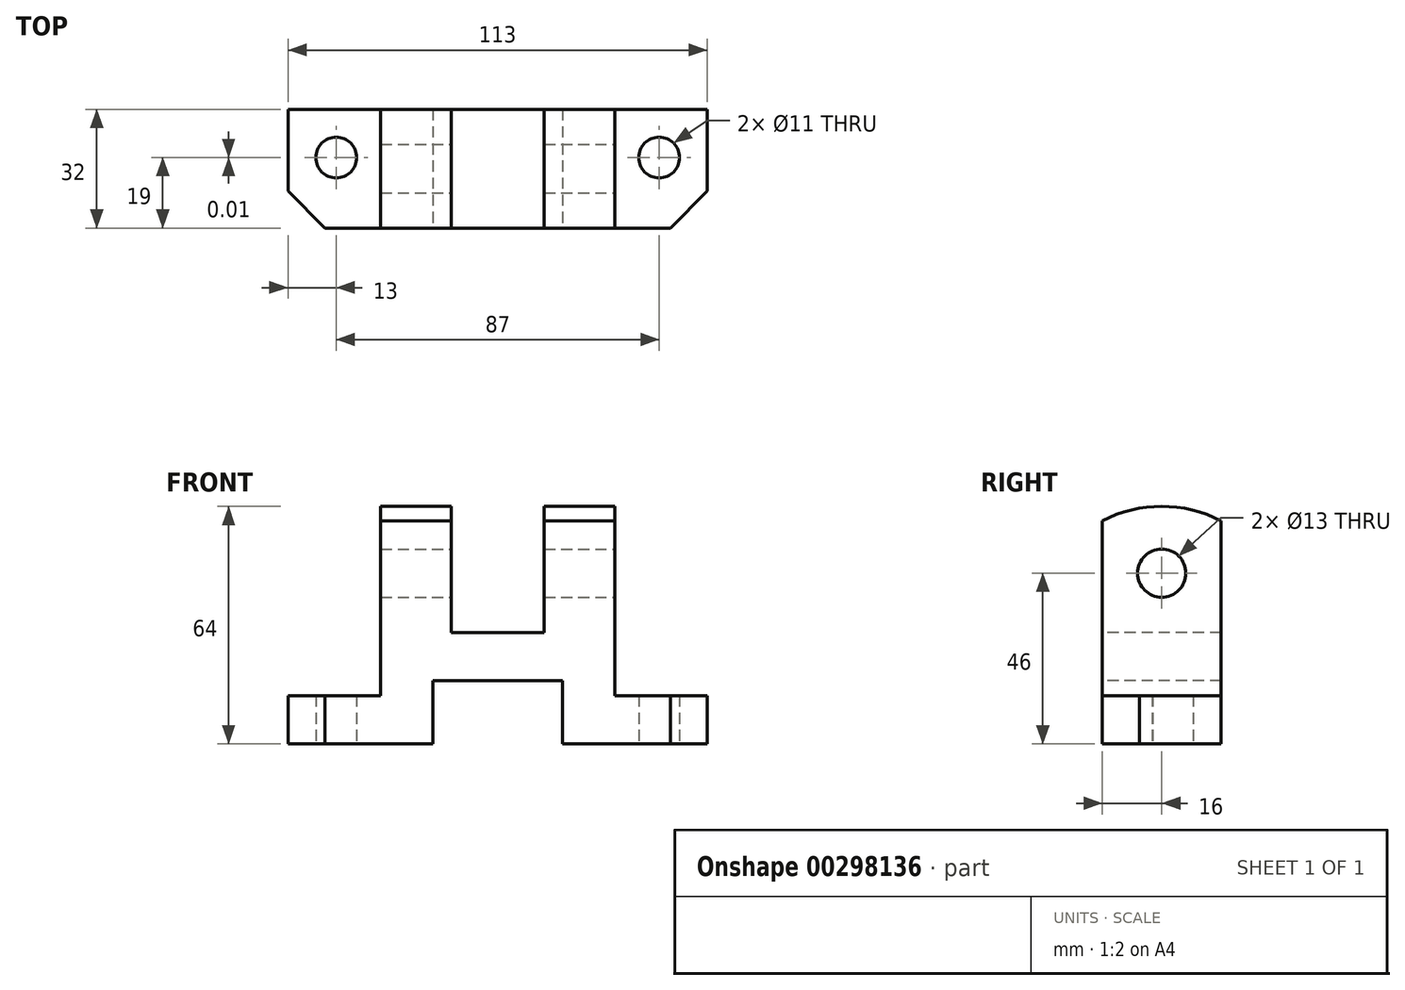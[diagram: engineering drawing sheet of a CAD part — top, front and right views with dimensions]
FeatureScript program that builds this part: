
annotation { "Feature Type Name" : "Feature", "Feature Type Description" : "" }
export const myFeature = defineFeature(function(context is Context, id is Id, definition is map)
    precondition{}
    {
        {
            var Q0;
            Q0=qCreatedBy(makeId("Front.planeOp"),FACE);
            var sketch = newSketch(context, id + "F0", { "sketchPlane" : qUnion([Q0])});
            skLineSegment(sketch, "E0", {"start": v(0, 0) * mm, "end": v(113, 0) * mm});
            skLineSegment(sketch, "E1", {"start": v(113, 0) * mm, "end": v(113, 64) * mm});
            skLineSegment(sketch, "E2", {"start": v(113, 64) * mm, "end": v(0, 64) * mm});
            skLineSegment(sketch, "E3", {"start": v(0, 64) * mm, "end": v(0, 0) * mm});
            skSolve(sketch);
        }
        {
            var Q0;
            Q0 = qSketchRegion(id + "F0", true);
            extrude(context, id + "F1", {"entities" : qUnion([Q0]), "depth" : 32 * mm});
        }
        {
            var Q0;
            Q0=makeQuery(id+"F1.opExtrude","CAP_FACE",FACE,{"disambiguationData":[OSD([sQuery(id+"F0.wireOp",EDGE,"E0"),sQuery(id+"F0.wireOp",EDGE,"E1"),sQuery(id+"F0.wireOp",EDGE,"E2"),sQuery(id+"F0.wireOp",EDGE,"E3")])],"isStart":false});
            var sketch = newSketch(context, id + "F2", { "sketchPlane" : qUnion([Q0])});
            skLineSegment(sketch, "E4", {"start": v(56.5, 94.84) * mm, "end": v(56.5, -26.19) * mm, "construction": true});
            skPoint(sketch, "E4.startSnap0", {"position": v(56.5, 64) * mm});
            skLineSegment(sketch, "E5", {"start": v(56.5, 0) * mm, "end": v(39, 0) * mm});
            skLineSegment(sketch, "E6", {"start": v(39, 0) * mm, "end": v(39, 17) * mm});
            skLineSegment(sketch, "E7", {"start": v(39, 17) * mm, "end": v(56.5, 17) * mm});
            skLineSegment(sketch, "E8", {"start": v(56.5, 17) * mm, "end": v(56.5, 0) * mm});
            skLineSegment(sketch, "E9.MirrorCS", {"start": v(74, 0) * mm, "end": v(74, 17) * mm});
            skLineSegment(sketch, "E10.MirrorCS", {"start": v(74, 17) * mm, "end": v(56.5, 17) * mm});
            skLineSegment(sketch, "E11.MirrorCS", {"start": v(56.5, 0) * mm, "end": v(74, 0) * mm});
            skLineSegment(sketch, "E12", {"start": v(56.5, 64) * mm, "end": v(44, 64) * mm});
            skLineSegment(sketch, "E13", {"start": v(44, 64) * mm, "end": v(44, 30) * mm});
            skLineSegment(sketch, "E14", {"start": v(44, 30) * mm, "end": v(56.5, 30) * mm});
            skLineSegment(sketch, "E15", {"start": v(56.5, 30) * mm, "end": v(56.5, 64) * mm});
            skLineSegment(sketch, "E16.MirrorCS", {"start": v(56.5, 64) * mm, "end": v(69, 64) * mm});
            skLineSegment(sketch, "E17.MirrorCS", {"start": v(69, 64) * mm, "end": v(69, 30) * mm});
            skLineSegment(sketch, "E18.MirrorCS", {"start": v(69, 30) * mm, "end": v(56.5, 30) * mm});
            skLineSegment(sketch, "E19", {"start": v(25, 64) * mm, "end": v(25, 13) * mm});
            skLineSegment(sketch, "E20", {"start": v(25, 13) * mm, "end": v(0, 13) * mm});
            skLineSegment(sketch, "E21", {"start": v(0, 13) * mm, "end": v(0, 64) * mm});
            skLineSegment(sketch, "E22", {"start": v(0, 64) * mm, "end": v(25, 64) * mm});
            skLineSegment(sketch, "E23.MirrorCS", {"start": v(88, 64) * mm, "end": v(88, 13) * mm});
            skLineSegment(sketch, "E24.MirrorCS", {"start": v(113, 64) * mm, "end": v(88, 64) * mm});
            skLineSegment(sketch, "E25.MirrorCS", {"start": v(113, 13) * mm, "end": v(113, 64) * mm});
            skLineSegment(sketch, "E26.MirrorCS", {"start": v(88, 13) * mm, "end": v(113, 13) * mm});
            skSolve(sketch);
        }
        {
            var Q0;
            Q0 = qSketchRegion(id + "F2", true);
            extrude(context, id + "F3", {"entities" : qUnion([Q0]), "operationType" : NewBodyOperationType.REMOVE, "endBound" : BoundingType.THROUGH_ALL, "oppositeDirection" : true, "depth" : 25 * mm});
        }
        {
            var Q0;
            Q0=makeQuery(id+"F3.boolean.opBoolean","COPY",FACE,{"derivedFrom":makeQuery(id+"F3.opExtrude","SWEPT_FACE",FACE,{"disambiguationData":[OSD([sQuery(id+"F2.wireOp",EDGE,"E23.MirrorCS")])]})});
            var sketch = newSketch(context, id + "F4", { "sketchPlane" : qUnion([Q0])});
            skArc(sketch, "E27", {"start": v(0, 60.13) * mm, "mid": v(-16, 64) * mm, "end": v(-32, 60.13) * mm});
            skLineSegment(sketch, "E28", {"start": v(-32, 60.13) * mm, "end": v(-32, 64) * mm});
            skLineSegment(sketch, "E29", {"start": v(-32, 64) * mm, "end": v(0, 64) * mm});
            skLineSegment(sketch, "E30", {"start": v(0, 64) * mm, "end": v(0, 60.13) * mm});
            skSolve(sketch);
        }
        {
            var Q0;
            {var subQ0=sQuery(id+"F4.wireOp",EDGE,"E28");Q0=makeQuery(id+"F4.imprint","IMPRINT",FACE,{"disambiguationData":[TD([[makeQuery(id+"F4.imprint","IMPRINT",EDGE,{"derivedFrom":subQ0}),1.0]])]});}
            var Q1;
            {var subQ0=sQuery(id+"F4.wireOp",EDGE,"E30");Q1=makeQuery(id+"F4.imprint","IMPRINT",FACE,{"disambiguationData":[TD([[makeQuery(id+"F4.imprint","IMPRINT",EDGE,{"derivedFrom":subQ0}),-1.0]])]});}
            extrude(context, id + "F5", {"entities" : qUnion([Q0, Q1]), "operationType" : NewBodyOperationType.REMOVE, "endBound" : BoundingType.THROUGH_ALL, "oppositeDirection" : true, "depth" : 25 * mm});
        }
        {
            var Q0;
            Q0=qCreatedBy(makeId("Top.planeOp"),FACE);
            var sketch = newSketch(context, id + "F6", { "sketchPlane" : qUnion([Q0])});
            skLineSegment(sketch, "E31", {"start": v(0, -22) * mm, "end": v(10, -32) * mm});
            skLineSegment(sketch, "E32", {"start": v(10, -32) * mm, "end": v(0, -32) * mm});
            skLineSegment(sketch, "E33", {"start": v(0, -32) * mm, "end": v(0, -22) * mm});
            skLineSegment(sketch, "E34", {"start": v(113, -22) * mm, "end": v(103, -32) * mm});
            skLineSegment(sketch, "E35", {"start": v(103, -32) * mm, "end": v(113, -32) * mm});
            skLineSegment(sketch, "E36", {"start": v(113, -32) * mm, "end": v(113, -22) * mm});
            skCircle(sketch, "E37", {"center": v(13, -13) * mm, "radius": 5.5 * mm});
            skCircle(sketch, "E38", {"center": v(100, -13) * mm, "radius": 5.5 * mm});
            skSolve(sketch);
        }
        {
            var Q0;
            Q0 = qSketchRegion(id + "F6", true);
            extrude(context, id + "F7", {"entities" : qUnion([Q0]), "operationType" : NewBodyOperationType.REMOVE, "endBound" : BoundingType.THROUGH_ALL, "depth" : 25 * mm});
        }
        {
            var Q0;
            Q0=makeQuery(id+"F3.boolean.opBoolean","COPY",FACE,{"derivedFrom":makeQuery(id+"F3.opExtrude","SWEPT_FACE",FACE,{"disambiguationData":[OSD([sQuery(id+"F2.wireOp",EDGE,"E23.MirrorCS")])]})});
            var sketch = newSketch(context, id + "F8", { "sketchPlane" : qUnion([Q0])});
            skCircle(sketch, "E39", {"center": v(-16, 46) * mm, "radius": 6.5 * mm});
            skSolve(sketch);
        }
        {
            var Q0;
            Q0 = qSketchRegion(id + "F8", true);
            extrude(context, id + "F9", {"entities" : qUnion([Q0]), "operationType" : NewBodyOperationType.REMOVE, "endBound" : BoundingType.THROUGH_ALL, "oppositeDirection" : true, "depth" : 25 * mm});
        }
    });
